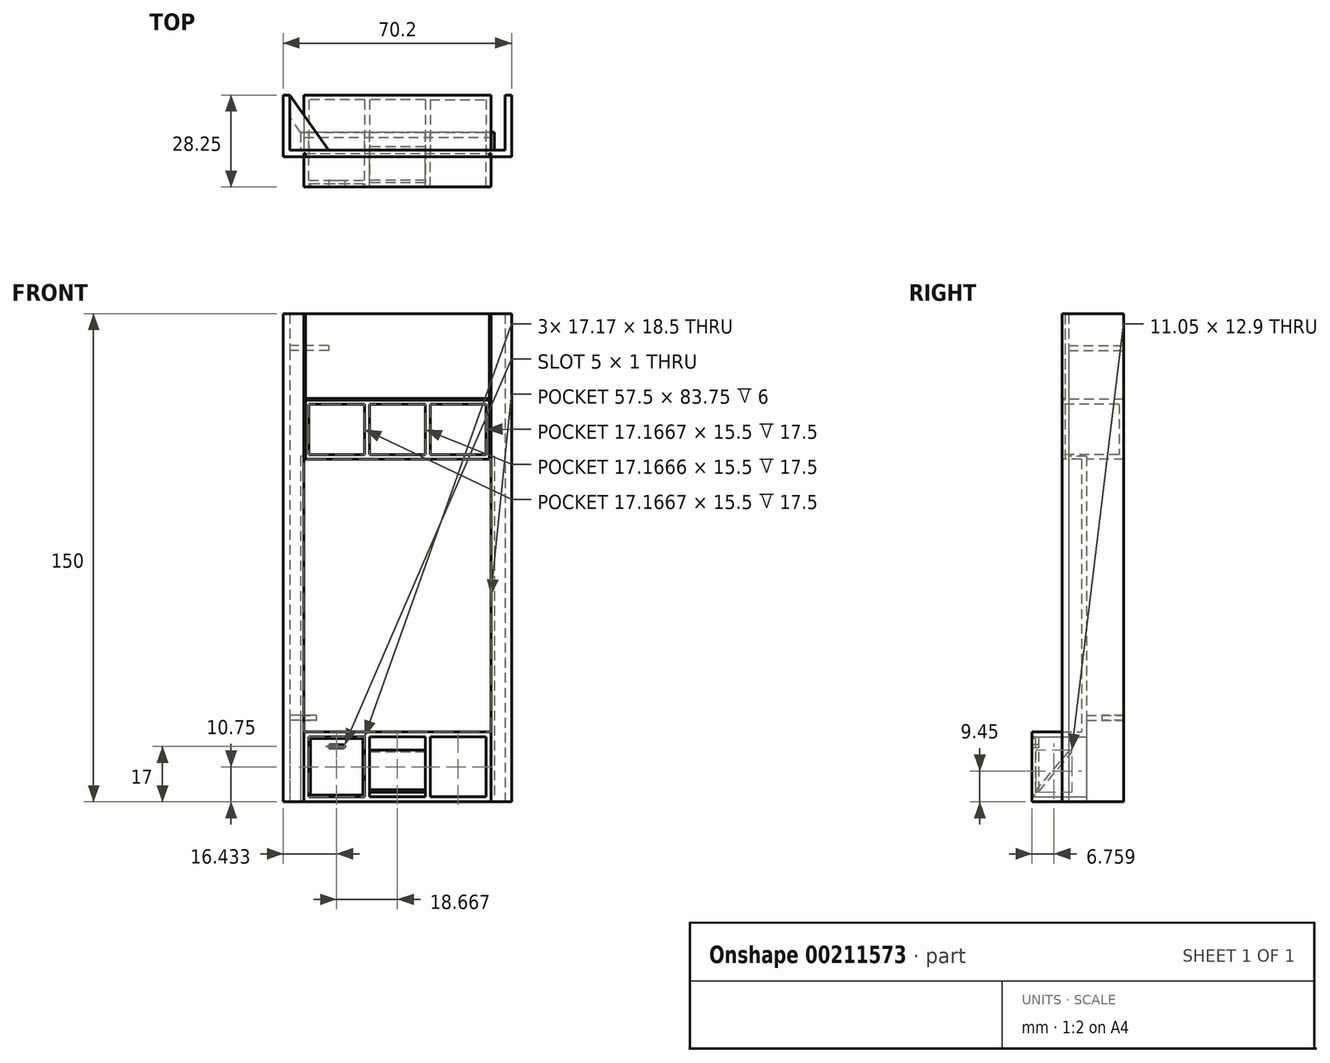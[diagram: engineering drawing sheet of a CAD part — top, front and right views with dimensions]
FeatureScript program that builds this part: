
annotation { "Feature Type Name" : "Feature", "Feature Type Description" : "" }
export const myFeature = defineFeature(function(context is Context, id is Id, definition is map)
    precondition{}
    {
        {
            var Q0;
            Q0=qCreatedBy(makeId("Front.planeOp"),FACE);
            var sketch = newSketch(context, id + "F0", { "sketchPlane" : qUnion([Q0])});
            skLineSegment(sketch, "E0.bottom", {"start": v(28.75, 0) * mm, "end": v(-28.75, 0) * mm});
            skLineSegment(sketch, "E0.top", {"start": v(28.75, 21.5) * mm, "end": v(-28.75, 21.5) * mm});
            skLineSegment(sketch, "E0.left", {"start": v(28.75, 0) * mm, "end": v(28.75, 21.5) * mm});
            skLineSegment(sketch, "E0.right", {"start": v(-28.75, 0) * mm, "end": v(-28.75, 21.5) * mm});
            skPoint(sketch, "E0.middle", {"position": v(0, 10.75) * mm});
            skLineSegment(sketch, "E1.bottom", {"start": v(-27.25, 20) * mm, "end": v(-10.08, 20) * mm});
            skLineSegment(sketch, "E1.top", {"start": v(-27.25, 1.5) * mm, "end": v(-10.08, 1.5) * mm});
            skLineSegment(sketch, "E1.left", {"start": v(-27.25, 20) * mm, "end": v(-27.25, 1.5) * mm});
            skLineSegment(sketch, "E1.right", {"start": v(-10.08, 20) * mm, "end": v(-10.08, 1.5) * mm});
            skLineSegment(sketch, "E2.bottom", {"start": v(-8.58, 20) * mm, "end": v(8.58, 20) * mm});
            skLineSegment(sketch, "E2.top", {"start": v(-8.58, 1.5) * mm, "end": v(8.58, 1.5) * mm});
            skLineSegment(sketch, "E2.left", {"start": v(-8.58, 20) * mm, "end": v(-8.58, 1.5) * mm});
            skLineSegment(sketch, "E2.right", {"start": v(8.58, 20) * mm, "end": v(8.58, 1.5) * mm});
            skLineSegment(sketch, "E3.bottom", {"start": v(10.08, 20) * mm, "end": v(27.25, 20) * mm});
            skLineSegment(sketch, "E3.top", {"start": v(10.08, 1.5) * mm, "end": v(27.25, 1.5) * mm});
            skLineSegment(sketch, "E3.left", {"start": v(10.08, 20) * mm, "end": v(10.08, 1.5) * mm});
            skLineSegment(sketch, "E3.right", {"start": v(27.25, 20) * mm, "end": v(27.25, 1.5) * mm});
            skPoint(sketch, "E4", {"position": v(0, 1.5) * mm});
            skSolve(sketch);
        }
        {
            var Q0;
            Q0=makeQuery(id+"F0.imprint","IMPRINT",FACE,{"disambiguationData":[TD([[makeQuery(id+"F0.imprint","IMPRINT",EDGE,{"derivedFrom":sQuery(id+"F0.wireOp",EDGE,"E0.bottom")}),-1.0]])]});
            extrude(context, id + "F1", {"entities" : qUnion([Q0]), "depth" : (335 / 20) * mm});
        }
        {
            var Q0;
            Q0=makeQuery(id+"F1.opExtrude","CAP_FACE",FACE,{"disambiguationData":[OSD([sQuery(id+"F0.wireOp",EDGE,"E0.bottom"),sQuery(id+"F0.wireOp",EDGE,"E0.top"),sQuery(id+"F0.wireOp",EDGE,"E0.left"),sQuery(id+"F0.wireOp",EDGE,"E0.right"),sQuery(id+"F0.wireOp",EDGE,"E1.bottom"),sQuery(id+"F0.wireOp",EDGE,"E1.top"),sQuery(id+"F0.wireOp",EDGE,"E1.left"),sQuery(id+"F0.wireOp",EDGE,"E1.right"),sQuery(id+"F0.wireOp",EDGE,"E2.bottom"),sQuery(id+"F0.wireOp",EDGE,"E2.top"),sQuery(id+"F0.wireOp",EDGE,"E2.left"),sQuery(id+"F0.wireOp",EDGE,"E2.right"),sQuery(id+"F0.wireOp",EDGE,"E3.bottom"),sQuery(id+"F0.wireOp",EDGE,"E3.top"),sQuery(id+"F0.wireOp",EDGE,"E3.left"),sQuery(id+"F0.wireOp",EDGE,"E3.right")])],"isStart":false});
            var sketch = newSketch(context, id + "F2", { "sketchPlane" : qUnion([Q0])});
            skLineSegment(sketch, "E5.0", {"start": v(-27.25, 20) * mm, "end": v(-10.08, 20) * mm});
            skLineSegment(sketch, "E6.0", {"start": v(-27.25, 20) * mm, "end": v(-27.25, 1.5) * mm});
            skLineSegment(sketch, "E7.0", {"start": v(-27.25, 1.5) * mm, "end": v(-10.08, 1.5) * mm});
            skPoint(sketch, "E8.0", {"position": v(-10.08, 10.75) * mm});
            skLineSegment(sketch, "E9.0", {"start": v(-10.08, 20) * mm, "end": v(-10.08, 1.5) * mm});
            skSolve(sketch);
        }
        {
            var Q0;
            Q0=makeQuery(id+"F2.imprint","IMPRINT",FACE,{"disambiguationData":[TD([[makeQuery(id+"F2.imprint","IMPRINT",EDGE,{"derivedFrom":sQuery(id+"F2.wireOp",EDGE,"E5.0")}),-1.0]])]});
            extrude(context, id + "F3", {"entities" : qUnion([Q0]), "operationType" : NewBodyOperationType.ADD, "oppositeDirection" : true, "depth" : 2 * mm});
        }
        {
            var Q0;
            Q0=makeQuery(id+"F3.boolean.opBoolean","MERGE",FACE,{"derivedFrom":[makeQuery(id+"F1.opExtrude","CAP_FACE",FACE,{"disambiguationData":[OSD([sQuery(id+"F0.wireOp",EDGE,"E0.bottom"),sQuery(id+"F0.wireOp",EDGE,"E0.top"),sQuery(id+"F0.wireOp",EDGE,"E0.left"),sQuery(id+"F0.wireOp",EDGE,"E0.right"),sQuery(id+"F0.wireOp",EDGE,"E1.bottom"),sQuery(id+"F0.wireOp",EDGE,"E1.top"),sQuery(id+"F0.wireOp",EDGE,"E1.left"),sQuery(id+"F0.wireOp",EDGE,"E1.right"),sQuery(id+"F0.wireOp",EDGE,"E2.bottom"),sQuery(id+"F0.wireOp",EDGE,"E2.top"),sQuery(id+"F0.wireOp",EDGE,"E2.left"),sQuery(id+"F0.wireOp",EDGE,"E2.right"),sQuery(id+"F0.wireOp",EDGE,"E3.bottom"),sQuery(id+"F0.wireOp",EDGE,"E3.top"),sQuery(id+"F0.wireOp",EDGE,"E3.left"),sQuery(id+"F0.wireOp",EDGE,"E3.right")])],"isStart":false}),makeQuery(id+"F3.opExtrude","CAP_FACE",FACE,{"disambiguationData":[OSD([sQuery(id+"F2.wireOp",EDGE,"E5.0"),sQuery(id+"F2.wireOp",EDGE,"E6.0"),sQuery(id+"F2.wireOp",EDGE,"E7.0"),sQuery(id+"F2.wireOp",EDGE,"E9.0")])],"isStart":true})]});
            var sketch = newSketch(context, id + "F4", { "sketchPlane" : qUnion([Q0])});
            skLineSegment(sketch, "E10.0", {"start": v(-27.25, 20) * mm, "end": v(-10.08, 20) * mm});
            skLineSegment(sketch, "E10.1", {"start": v(-27.25, 20) * mm, "end": v(-27.25, 1.5) * mm});
            skLineSegment(sketch, "E10.2", {"start": v(-27.25, 1.5) * mm, "end": v(-10.08, 1.5) * mm});
            skLineSegment(sketch, "E10.3", {"start": v(-10.08, 20) * mm, "end": v(-10.08, 1.5) * mm});
            skLineSegment(sketch, "E11.0", {"start": v(-26.75, 19.5) * mm, "end": v(-10.58, 19.5) * mm});
            skLineSegment(sketch, "E11.1", {"start": v(-26.75, 19.5) * mm, "end": v(-26.75, 2) * mm});
            skLineSegment(sketch, "E11.2", {"start": v(-26.75, 2) * mm, "end": v(-10.58, 2) * mm});
            skLineSegment(sketch, "E11.3", {"start": v(-10.58, 19.5) * mm, "end": v(-10.58, 2) * mm});
            skSolve(sketch);
        }
        {
            var Q0;
            Q0=makeQuery(id+"F4.imprint","IMPRINT",FACE,{"disambiguationData":[TD([[makeQuery(id+"F4.imprint","IMPRINT",EDGE,{"derivedFrom":sQuery(id+"F4.wireOp",EDGE,"E10.0")}),-1.0]])]});
            extrude(context, id + "F5", {"entities" : qUnion([Q0]), "operationType" : NewBodyOperationType.REMOVE, "oppositeDirection" : true, "depth" : 1 * mm});
        }
        {
            var Q0;
            Q0=makeQuery(id+"F5.boolean.opBoolean","SPLIT",FACE,{"disambiguationData":[TD([makeQuery(id+"F5.opExtrude","SWEPT_FACE",FACE,{"disambiguationData":[OSD([sQuery(id+"F4.wireOp",EDGE,"E11.0")])]})])],"derivedFrom":makeQuery(id+"F3.boolean.opBoolean","MERGE",FACE,{"derivedFrom":[makeQuery(id+"F1.opExtrude","CAP_FACE",FACE,{"disambiguationData":[OSD([sQuery(id+"F0.wireOp",EDGE,"E0.bottom"),sQuery(id+"F0.wireOp",EDGE,"E0.top"),sQuery(id+"F0.wireOp",EDGE,"E0.left"),sQuery(id+"F0.wireOp",EDGE,"E0.right"),sQuery(id+"F0.wireOp",EDGE,"E1.bottom"),sQuery(id+"F0.wireOp",EDGE,"E1.top"),sQuery(id+"F0.wireOp",EDGE,"E1.left"),sQuery(id+"F0.wireOp",EDGE,"E1.right"),sQuery(id+"F0.wireOp",EDGE,"E2.bottom"),sQuery(id+"F0.wireOp",EDGE,"E2.top"),sQuery(id+"F0.wireOp",EDGE,"E2.left"),sQuery(id+"F0.wireOp",EDGE,"E2.right"),sQuery(id+"F0.wireOp",EDGE,"E3.bottom"),sQuery(id+"F0.wireOp",EDGE,"E3.top"),sQuery(id+"F0.wireOp",EDGE,"E3.left"),sQuery(id+"F0.wireOp",EDGE,"E3.right")])],"isStart":false}),makeQuery(id+"F3.opExtrude","CAP_FACE",FACE,{"disambiguationData":[OSD([sQuery(id+"F2.wireOp",EDGE,"E5.0"),sQuery(id+"F2.wireOp",EDGE,"E6.0"),sQuery(id+"F2.wireOp",EDGE,"E7.0"),sQuery(id+"F2.wireOp",EDGE,"E9.0")])],"isStart":true})]})});
            var sketch = newSketch(context, id + "F6", { "sketchPlane" : qUnion([Q0])});
            skLineSegment(sketch, "E12.bottom", {"start": v(-20.67, 17.5) * mm, "end": v(-16.67, 17.5) * mm});
            skLineSegment(sketch, "E12.top", {"start": v(-20.67, 16.5) * mm, "end": v(-16.67, 16.5) * mm});
            skLineSegment(sketch, "E12.left", {"start": v(-21.17, 17) * mm, "end": v(-21.17, 17) * mm});
            skLineSegment(sketch, "E12.right", {"start": v(-16.17, 17) * mm, "end": v(-16.17, 17) * mm});
            skPoint(sketch, "E13", {"position": v(-18.67, 17.5) * mm});
            skPoint(sketch, "E14.visualSharp", {"position": v(-21.17, 17.5) * mm});
            skArc(sketch, "E14.filletArc", {"start": v(-20.67, 17.5) * mm, "mid": v(-21.02, 17.35) * mm, "end": v(-21.17, 17) * mm});
            skPoint(sketch, "E15.visualSharp", {"position": v(-21.17, 16.5) * mm});
            skArc(sketch, "E15.filletArc", {"start": v(-21.17, 17) * mm, "mid": v(-21.02, 16.65) * mm, "end": v(-20.67, 16.5) * mm});
            skPoint(sketch, "E16.visualSharp", {"position": v(-16.17, 16.5) * mm});
            skArc(sketch, "E16.filletArc", {"start": v(-16.67, 16.5) * mm, "mid": v(-16.31, 16.65) * mm, "end": v(-16.17, 17) * mm});
            skPoint(sketch, "E17.visualSharp", {"position": v(-16.17, 17.5) * mm});
            skArc(sketch, "E17.filletArc", {"start": v(-16.17, 17) * mm, "mid": v(-16.31, 17.35) * mm, "end": v(-16.67, 17.5) * mm});
            skSolve(sketch);
        }
        {
            var Q0;
            Q0=makeQuery(id+"F6.imprint","IMPRINT",FACE,{"disambiguationData":[TD([[makeQuery(id+"F6.imprint","IMPRINT",EDGE,{"derivedFrom":sQuery(id+"F6.wireOp",EDGE,"E12.bottom")}),-1.0]])]});
            extrude(context, id + "F7", {"entities" : qUnion([Q0]), "operationType" : NewBodyOperationType.REMOVE, "endBound" : BoundingType.THROUGH_ALL, "oppositeDirection" : true, "depth" : 25 * mm});
        }
        {
            var Q0;
            Q0=makeQuery(id+"F1.opExtrude","SWEPT_FACE",FACE,{"disambiguationData":[OSD([sQuery(id+"F0.wireOp",EDGE,"E2.left")])]});
            var sketch = newSketch(context, id + "F8", { "sketchPlane" : qUnion([Q0])});
            skLineSegment(sketch, "E18", {"start": v(-14.75, 3) * mm, "end": v(-4.47, 15.26) * mm});
            skLineSegment(sketch, "E19", {"start": v(-4.47, 15.26) * mm, "end": v(-5.23, 15.9) * mm});
            skLineSegment(sketch, "E20", {"start": v(-5.23, 15.9) * mm, "end": v(-15.52, 3.64) * mm});
            skLineSegment(sketch, "E21", {"start": v(-15.52, 3.64) * mm, "end": v(-14.75, 3) * mm});
            skSolve(sketch);
        }
        {
            var Q0;
            Q0=makeQuery(id+"F8.imprint","IMPRINT",FACE,{"disambiguationData":[TD([[makeQuery(id+"F8.imprint","IMPRINT",EDGE,{"derivedFrom":sQuery(id+"F8.wireOp",EDGE,"E18")}),1.0]])]});
            extrude(context, id + "F9", {"entities" : qUnion([Q0]), "operationType" : NewBodyOperationType.ADD, "endBound" : BoundingType.UP_TO_NEXT, "depth" : 25 * mm});
        }
        {
            var Q0;
            Q0=makeQuery(id+"F1.opExtrude","SWEPT_FACE",FACE,{"disambiguationData":[OSD([sQuery(id+"F0.wireOp",EDGE,"E0.top")])]});
            var sketch = newSketch(context, id + "F10", { "sketchPlane" : qUnion([Q0])});
            skLineSegment(sketch, "E22.bottom", {"start": v(-28.75, 0) * mm, "end": v(28.75, 0) * mm});
            skLineSegment(sketch, "E22.top", {"start": v(-28.75, -1.5) * mm, "end": v(28.75, -1.5) * mm});
            skLineSegment(sketch, "E22.left", {"start": v(-28.75, 0) * mm, "end": v(-28.75, -1.5) * mm});
            skLineSegment(sketch, "E22.right", {"start": v(28.75, 0) * mm, "end": v(28.75, -1.5) * mm});
            skSolve(sketch);
        }
        {
            var Q0;
            Q0=makeQuery(id+"F10.imprint","IMPRINT",FACE,{"disambiguationData":[TD([[makeQuery(id+"F10.imprint","IMPRINT",EDGE,{"derivedFrom":sQuery(id+"F10.wireOp",EDGE,"E22.bottom")}),1.0]])]});
            extrude(context, id + "F11", {"entities" : qUnion([Q0]), "operationType" : NewBodyOperationType.ADD, "depth" : (1675 / 20) * mm});
        }
        {
            var Q0;
            Q0=qCreatedBy(makeId("Front.planeOp"),FACE);
            cPlane(context, id + "F12", {"entities" : qUnion([Q0]), "cplaneType" : CPlaneType.OFFSET, "offset" : (150 / 20) * mm, "width" : 150 * mm, "height" : 150 * mm});
        }
        {
            var Q0;
            Q0=qCreatedBy(id+"F12.planeOp",FACE);
            var sketch = newSketch(context, id + "F13", { "sketchPlane" : qUnion([Q0])});
            skLineSegment(sketch, "E23.bottom", {"start": v(-28.75, 105.25) * mm, "end": v(28.75, 105.25) * mm});
            skLineSegment(sketch, "E23.top", {"start": v(-28.75, 123.75) * mm, "end": v(28.75, 123.75) * mm});
            skLineSegment(sketch, "E23.left", {"start": v(-28.75, 105.25) * mm, "end": v(-28.75, 123.75) * mm});
            skLineSegment(sketch, "E23.right", {"start": v(28.75, 105.25) * mm, "end": v(28.75, 123.75) * mm});
            skPoint(sketch, "E24.middle", {"position": v(0, 114.5) * mm});
            skSolve(sketch);
        }
        {
            var Q0;
            Q0=makeQuery(id+"F13.imprint","IMPRINT",FACE,{"disambiguationData":[TD([[makeQuery(id+"F13.imprint","IMPRINT",EDGE,{"derivedFrom":sQuery(id+"F13.wireOp",EDGE,"E23.bottom")}),1.0]])]});
            extrude(context, id + "F14", {"entities" : qUnion([Q0]), "operationType" : NewBodyOperationType.ADD, "oppositeDirection" : true, "depth" : (380 / 20) * mm});
        }
        {
            var Q0;
            Q0=makeQuery(id+"F14.opExtrude","CAP_FACE",FACE,{"disambiguationData":[OSD([sQuery(id+"F13.wireOp",EDGE,"E23.bottom"),sQuery(id+"F13.wireOp",EDGE,"E23.top"),sQuery(id+"F13.wireOp",EDGE,"E23.left"),sQuery(id+"F13.wireOp",EDGE,"E23.right")])],"isStart":true});
            var sketch = newSketch(context, id + "F15", { "sketchPlane" : qUnion([Q0])});
            skLineSegment(sketch, "E25.bottom", {"start": v(8.58, 106.75) * mm, "end": v(-8.58, 106.75) * mm});
            skLineSegment(sketch, "E25.top", {"start": v(8.58, 122.25) * mm, "end": v(-8.58, 122.25) * mm});
            skLineSegment(sketch, "E25.left", {"start": v(8.58, 106.75) * mm, "end": v(8.58, 122.25) * mm});
            skLineSegment(sketch, "E25.right", {"start": v(-8.58, 106.75) * mm, "end": v(-8.58, 122.25) * mm});
            skPoint(sketch, "E25.middle", {"position": v(0, 114.5) * mm});
            skLineSegment(sketch, "E26.bottom", {"start": v(10.08, 122.25) * mm, "end": v(27.25, 122.25) * mm});
            skLineSegment(sketch, "E26.top", {"start": v(10.08, 106.75) * mm, "end": v(27.25, 106.75) * mm});
            skLineSegment(sketch, "E26.left", {"start": v(10.08, 122.25) * mm, "end": v(10.08, 106.75) * mm});
            skLineSegment(sketch, "E26.right", {"start": v(27.25, 122.25) * mm, "end": v(27.25, 106.75) * mm});
            skLineSegment(sketch, "E27.bottom", {"start": v(-10.08, 122.25) * mm, "end": v(-27.25, 122.25) * mm});
            skLineSegment(sketch, "E27.top", {"start": v(-10.08, 106.75) * mm, "end": v(-27.25, 106.75) * mm});
            skLineSegment(sketch, "E27.left", {"start": v(-10.08, 122.25) * mm, "end": v(-10.08, 106.75) * mm});
            skLineSegment(sketch, "E27.right", {"start": v(-27.25, 122.25) * mm, "end": v(-27.25, 106.75) * mm});
            skSolve(sketch);
        }
        {
            var Q0;
            Q0=makeQuery(id+"F15.imprint","IMPRINT",FACE,{"disambiguationData":[TD([[makeQuery(id+"F15.imprint","IMPRINT",EDGE,{"derivedFrom":sQuery(id+"F15.wireOp",EDGE,"E27.bottom")}),1.0]])]});
            var Q1;
            Q1=makeQuery(id+"F15.imprint","IMPRINT",FACE,{"disambiguationData":[TD([[makeQuery(id+"F15.imprint","IMPRINT",EDGE,{"derivedFrom":sQuery(id+"F15.wireOp",EDGE,"E25.bottom")}),-1.0]])]});
            var Q2;
            Q2=makeQuery(id+"F15.imprint","IMPRINT",FACE,{"disambiguationData":[TD([[makeQuery(id+"F15.imprint","IMPRINT",EDGE,{"derivedFrom":sQuery(id+"F15.wireOp",EDGE,"E26.bottom")}),-1.0]])]});
            extrude(context, id + "F16", {"entities" : qUnion([Q0, Q1, Q2]), "operationType" : NewBodyOperationType.REMOVE, "oppositeDirection" : true, "depth" : 17.5 * mm});
        }
        {
            var Q0;
            Q0=qCreatedBy(makeId("Right.planeOp"),FACE);
            var sketch = newSketch(context, id + "F17", { "sketchPlane" : qUnion([Q0])});
            skLineSegment(sketch, "E28.bottom", {"start": v(-7.5, 123.75) * mm, "end": v(-5.5, 123.75) * mm});
            skLineSegment(sketch, "E28.top", {"start": v(-7.5, 150) * mm, "end": v(-5.5, 150) * mm});
            skLineSegment(sketch, "E28.left", {"start": v(-7.5, 123.75) * mm, "end": v(-7.5, 150) * mm});
            skLineSegment(sketch, "E28.right", {"start": v(-5.5, 123.75) * mm, "end": v(-5.5, 150) * mm});
            skSolve(sketch);
        }
        {
            var Q0;
            Q0=makeQuery(id+"F17.imprint","IMPRINT",FACE,{"disambiguationData":[TD([[makeQuery(id+"F17.imprint","IMPRINT",EDGE,{"derivedFrom":sQuery(id+"F17.wireOp",EDGE,"E28.bottom")}),1.0]])]});
            var Q1;
            Q1=makeQuery(id+"F14.opExtrude","CAP_VERTEX",VERTEX,{"disambiguationData":[OSD([sQuery(id+"F13.wireOp",EDGE,"E23.top"),sQuery(id+"F13.wireOp",EDGE,"E23.right")])],"isStart":true});
            var Q2;
            Q2=makeQuery(id+"F14.opExtrude","CAP_VERTEX",VERTEX,{"disambiguationData":[OSD([sQuery(id+"F13.wireOp",EDGE,"E23.top"),sQuery(id+"F13.wireOp",EDGE,"E23.left")])],"isStart":true});
            extrude(context, id + "F18", {"entities" : qUnion([Q0]), "operationType" : NewBodyOperationType.ADD, "endBound" : BoundingType.UP_TO_VERTEX, "endBoundEntityVertex" : qUnion([Q1]), "depth" : 25 * mm, "hasSecondDirection" : true, "secondDirectionBound" : SecondDirectionBoundingType.UP_TO_VERTEX, "secondDirectionOppositeDirection" : true, "secondDirectionBoundEntityVertex" : qUnion([Q2]), "secondDirectionDepth" : 25 * mm});
        }
        {
            var Q0;
            Q0=qCreatedBy(makeId("Top.planeOp"),FACE);
            var sketch = newSketch(context, id + "F19", { "sketchPlane" : qUnion([Q0])});
            skLineSegment(sketch, "E29.bottom", {"start": v(-28.75, -7.5) * mm, "end": v(-35.1, -7.5) * mm});
            skLineSegment(sketch, "E29.right", {"start": v(-35.1, -7.5) * mm, "end": v(-35.1, 11.5) * mm});
            skLineSegment(sketch, "E30", {"start": v(-35.1, 11.5) * mm, "end": v(-33.1, 11.5) * mm});
            skLineSegment(sketch, "E31", {"start": v(-33.1, 11.5) * mm, "end": v(-33.1, -5.5) * mm});
            skLineSegment(sketch, "E32", {"start": v(-33.1, -5.5) * mm, "end": v(-28.75, -5.5) * mm});
            skLineSegment(sketch, "E33", {"start": v(-28.75, -5.5) * mm, "end": v(-28.75, -7.5) * mm});
            skLineSegment(sketch, "E34", {"start": v(0, 0) * mm, "end": v(0, 27.28) * mm, "construction": true});
            skLineSegment(sketch, "E35.MirrorCS", {"start": v(35.1, 11.5) * mm, "end": v(33.1, 11.5) * mm});
            skLineSegment(sketch, "E36.MirrorCS", {"start": v(33.1, -5.5) * mm, "end": v(28.75, -5.5) * mm});
            skLineSegment(sketch, "E37.MirrorCS", {"start": v(28.75, -5.5) * mm, "end": v(28.75, -7.5) * mm});
            skLineSegment(sketch, "E38.MirrorCS", {"start": v(35.1, -7.5) * mm, "end": v(35.1, 11.5) * mm});
            skLineSegment(sketch, "E39.MirrorCS", {"start": v(28.75, -7.5) * mm, "end": v(35.1, -7.5) * mm});
            skLineSegment(sketch, "E40.MirrorCS", {"start": v(33.1, 11.5) * mm, "end": v(33.1, -5.5) * mm});
            skSolve(sketch);
        }
        {
            var Q0;
            Q0=makeQuery(id+"F19.imprint","IMPRINT",FACE,{"disambiguationData":[TD([[makeQuery(id+"F19.imprint","IMPRINT",EDGE,{"derivedFrom":sQuery(id+"F19.wireOp",EDGE,"E29.bottom")}),-1.0]])]});
            var Q1;
            Q1=makeQuery(id+"F19.imprint","IMPRINT",FACE,{"disambiguationData":[TD([[makeQuery(id+"F19.imprint","IMPRINT",EDGE,{"derivedFrom":sQuery(id+"F19.wireOp",EDGE,"E35.MirrorCS")}),1.0]])]});
            var Q2;
            Q2=makeQuery(id+"F18.opExtrude","CAP_VERTEX",VERTEX,{"disambiguationData":[OSD([sQuery(id+"F17.wireOp",EDGE,"E28.top"),sQuery(id+"F17.wireOp",EDGE,"E28.left"),dummyQuery(id+"F18.secondVertexPlane.planeOp",FACE)])],"isStart":true});
            extrude(context, id + "F20", {"entities" : qUnion([Q0, Q1]), "operationType" : NewBodyOperationType.ADD, "endBound" : BoundingType.UP_TO_VERTEX, "endBoundEntityVertex" : qUnion([Q2]), "depth" : 150 * mm});
        }
        {
            var Q0;
            Q0=qCreatedBy(makeId("Top.planeOp"),FACE);
            var sketch = newSketch(context, id + "F21", { "sketchPlane" : qUnion([Q0])});
            skLineSegment(sketch, "E41.bottom", {"start": v(-28.75, 0) * mm, "end": v(-29.75, 0) * mm});
            skLineSegment(sketch, "E41.top", {"start": v(-28.75, -5.5) * mm, "end": v(-29.75, -5.5) * mm});
            skLineSegment(sketch, "E41.left", {"start": v(-28.75, 0) * mm, "end": v(-28.75, -5.5) * mm});
            skLineSegment(sketch, "E41.right", {"start": v(-29.75, 0) * mm, "end": v(-29.75, -5.5) * mm});
            skLineSegment(sketch, "E42", {"start": v(0, 1.92) * mm, "end": v(0, 23.31) * mm, "construction": true});
            skLineSegment(sketch, "E43.MirrorCS", {"start": v(28.75, -5.5) * mm, "end": v(29.75, -5.5) * mm});
            skLineSegment(sketch, "E44.MirrorCS", {"start": v(28.75, 0) * mm, "end": v(29.75, 0) * mm});
            skLineSegment(sketch, "E45.MirrorCS", {"start": v(29.75, 0) * mm, "end": v(29.75, -5.5) * mm});
            skLineSegment(sketch, "E46.MirrorCS", {"start": v(28.75, 0) * mm, "end": v(28.75, -5.5) * mm});
            skSolve(sketch);
        }
        {
            var Q0;
            Q0=makeQuery(id+"F21.imprint","IMPRINT",FACE,{"disambiguationData":[TD([[makeQuery(id+"F21.imprint","IMPRINT",EDGE,{"derivedFrom":sQuery(id+"F21.wireOp",EDGE,"E41.bottom")}),1.0]])]});
            var Q1;
            Q1=makeQuery(id+"F21.imprint","IMPRINT",FACE,{"disambiguationData":[TD([[makeQuery(id+"F21.imprint","IMPRINT",EDGE,{"derivedFrom":sQuery(id+"F21.wireOp",EDGE,"E43.MirrorCS")}),1.0]])]});
            var Q2;
            {var subQ2=sQuery(id+"F13.wireOp",EDGE,"E23.bottom");Q2=makeQuery(id+"F14.boolean.opBoolean","SPLIT",FACE,{"disambiguationData":[TD([makeQuery(id+"F11.opExtrude","SWEPT_FACE",FACE,{"disambiguationData":[OSD([sQuery(id+"F10.wireOp",EDGE,"E22.top")])]})])],"derivedFrom":makeQuery(id+"F14.opExtrude","SWEPT_FACE",FACE,{"disambiguationData":[OSD([subQ2])]})});}
            extrude(context, id + "F22", {"entities" : qUnion([Q0, Q1]), "operationType" : NewBodyOperationType.ADD, "endBoundEntityFace" : qUnion([Q2]), "depth" : 106.2 * mm});
        }
        {
            var Q0;
            Q0=makeQuery(id+"F20.boolean.opBoolean","MERGE",FACE,{"derivedFrom":[makeQuery(id+"F18.boolean.opBoolean","MERGE",FACE,{"derivedFrom":[makeQuery(id+"F14.opExtrude","CAP_FACE",FACE,{"disambiguationData":[OSD([sQuery(id+"F13.wireOp",EDGE,"E23.bottom"),sQuery(id+"F13.wireOp",EDGE,"E23.top"),sQuery(id+"F13.wireOp",EDGE,"E23.left"),sQuery(id+"F13.wireOp",EDGE,"E23.right")])],"isStart":true}),makeQuery(id+"F18.opExtrude","SWEPT_FACE",FACE,{"disambiguationData":[OSD([sQuery(id+"F17.wireOp",EDGE,"E28.left")])]})]}),makeQuery(id+"F20.opExtrude","SWEPT_FACE",FACE,{"disambiguationData":[OSD([sQuery(id+"F19.wireOp",EDGE,"E29.bottom")])]}),makeQuery(id+"F20.opExtrude","SWEPT_FACE",FACE,{"disambiguationData":[OSD([sQuery(id+"F19.wireOp",EDGE,"E39.MirrorCS")])]})]});
            var sketch = newSketch(context, id + "F23", { "sketchPlane" : qUnion([Q0])});
            skLineSegment(sketch, "E47.bottom", {"start": v(28.75, 105.25) * mm, "end": v(28.25, 105.25) * mm});
            skLineSegment(sketch, "E47.top", {"start": v(28.75, 150) * mm, "end": v(28.25, 150) * mm});
            skLineSegment(sketch, "E47.left", {"start": v(28.75, 105.25) * mm, "end": v(28.75, 150) * mm});
            skLineSegment(sketch, "E47.right", {"start": v(28.25, 105.25) * mm, "end": v(28.25, 123.5) * mm});
            skLineSegment(sketch, "E48", {"start": v(0, 105.25) * mm, "end": v(0, 117.06) * mm, "construction": true});
            skLineSegment(sketch, "E49.MirrorCS", {"start": v(-28.75, 105.25) * mm, "end": v(-28.25, 105.25) * mm});
            skLineSegment(sketch, "E50.MirrorCS", {"start": v(-28.75, 150) * mm, "end": v(-28.25, 150) * mm});
            skLineSegment(sketch, "E51.MirrorCS", {"start": v(-28.25, 105.25) * mm, "end": v(-28.25, 123.5) * mm});
            skLineSegment(sketch, "E52.MirrorCS", {"start": v(-28.75, 105.25) * mm, "end": v(-28.75, 150) * mm});
            skLineSegment(sketch, "E53.bottom", {"start": v(-28.25, 123.5) * mm, "end": v(28.25, 123.5) * mm});
            skLineSegment(sketch, "E53.top", {"start": v(-28.25, 124) * mm, "end": v(28.25, 124) * mm});
            skLineSegment(sketch, "E54.trimOffspring", {"start": v(28.25, 124) * mm, "end": v(28.25, 150) * mm});
            skLineSegment(sketch, "E55.trimOffspring", {"start": v(-28.25, 124) * mm, "end": v(-28.25, 150) * mm});
            skSolve(sketch);
        }
        {
            var Q0;
            Q0=makeQuery(id+"F23.imprint","IMPRINT",FACE,{"disambiguationData":[TD([[makeQuery(id+"F23.imprint","IMPRINT",EDGE,{"derivedFrom":sQuery(id+"F23.wireOp",EDGE,"E47.bottom")}),1.0]])]});
            extrude(context, id + "F24", {"entities" : qUnion([Q0]), "operationType" : NewBodyOperationType.REMOVE, "oppositeDirection" : true, "depth" : 1 * mm});
        }
        {
            var Q0;
            Q0=makeQuery(id+"F14.opExtrude","SWEPT_FACE",FACE,{"disambiguationData":[OSD([sQuery(id+"F13.wireOp",EDGE,"E23.top")])]});
            cPlane(context, id + "F25", {"entities" : qUnion([Q0]), "cplaneType" : CPlaneType.OFFSET, "offset" : 15 * mm, "width" : 150 * mm, "height" : 150 * mm});
        }
        {
            var Q0;
            Q0=qCreatedBy(id+"F25.planeOp",FACE);
            var sketch = newSketch(context, id + "F26", { "sketchPlane" : qUnion([Q0])});
            skLineSegment(sketch, "E56", {"start": v(-33.1, 11.5) * mm, "end": v(-21.1, -5.5) * mm});
            skLineSegment(sketch, "E57", {"start": v(-21.1, -5.5) * mm, "end": v(-33.1, -5.5) * mm});
            skLineSegment(sketch, "E58", {"start": v(-33.1, -5.5) * mm, "end": v(-33.1, 11.5) * mm});
            skSolve(sketch);
        }
        {
            var Q0;
            Q0=makeQuery(id+"F26.imprint","IMPRINT",FACE,{"disambiguationData":[TD([[makeQuery(id+"F26.imprint","IMPRINT",EDGE,{"derivedFrom":sQuery(id+"F26.wireOp",EDGE,"E56")}),-1.0]])]});
            extrude(context, id + "F27", {"entities" : qUnion([Q0]), "operationType" : NewBodyOperationType.ADD, "depth" : 1.5 * mm});
        }
        {
            var Q0;
            Q0=qCreatedBy(makeId("Top.planeOp"),FACE);
            cPlane(context, id + "F28", {"entities" : qUnion([Q0]), "cplaneType" : CPlaneType.OFFSET, "offset" : 25 * mm, "width" : 150 * mm, "height" : 150 * mm});
        }
        {
            var Q0;
            Q0=qCreatedBy(id+"F28.planeOp",FACE);
            var sketch = newSketch(context, id + "F29", { "sketchPlane" : qUnion([Q0])});
            skLineSegment(sketch, "E59", {"start": v(-29.75, 0) * mm, "end": v(-24.98, 0) * mm});
            skLineSegment(sketch, "E60", {"start": v(-24.98, 0) * mm, "end": v(-33.1, 11.5) * mm});
            skLineSegment(sketch, "E61", {"start": v(-33.1, 11.5) * mm, "end": v(-33.1, 4.75) * mm});
            skLineSegment(sketch, "E62", {"start": v(-29.75, 0) * mm, "end": v(-33.1, 4.75) * mm});
            skSolve(sketch);
        }
        {
            var Q0;
            Q0=makeQuery(id+"F29.imprint","IMPRINT",FACE,{"disambiguationData":[TD([[makeQuery(id+"F29.imprint","IMPRINT",EDGE,{"derivedFrom":sQuery(id+"F29.wireOp",EDGE,"E59")}),1.0]])]});
            extrude(context, id + "F30", {"entities" : qUnion([Q0]), "operationType" : NewBodyOperationType.ADD, "depth" : 1.5 * mm});
        }
    });
